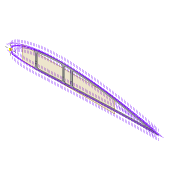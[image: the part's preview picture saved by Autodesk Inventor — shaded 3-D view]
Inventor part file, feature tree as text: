
AUTODESK INVENTOR PART (.ipt)
format: ipt  version: 2022 (Build 260153000, 153)  size: 489,984 bytes
history: native  units: mm
features: projected_geometry x8, extrude x7, sketch x7, shell x1, plane x1, chamfer x1
ambient origin geometry x8: Origin, YZ Plane, XZ Plane, XY Plane, X Axis, Y Axis, Z Axis, Center Point
bodies: Solid1 (feature_tree)
feature tree (25):
  extrude  "Extrusion1"  Depth=4.0mm
  shell  "Shell1"  Thickness=2.0mm
  extrude  "Extrusion8"  Depth=5.9mm
  extrude  "Extrusion3"  Depth=10.0mm TaperAngle=0.0deg
  extrude  "Extrusion4"  Depth=5.0mm
  extrude  "Extrusion5"  Depth=2.5mm
  plane  "Work Plane2"
  extrude  "Extrusion9"  Depth=1.6mm
  chamfer  "Chamfer1"  Distance=77.0mm
  extrude  "Extrusion12"  Depth=5.0mm
  sketch  "Sketch31"  dims[d37=5.0mm d38=1.6mm]
  sketch  "Sketch32"  dims[d40=2.5mm d62=77.0mm d63=5.0mm d64=2.0mm d65=0.0mm d66=2.5mm d67=12.0mm d68=80.0mm d69=20.0mm d70=0.5mm d71=10.0mm d72=0.0mm d75=3.0mm d76=3.0mm d77=2.0mm d78=45.0deg d80=0.0mm d81=1.0mm d82=1.0mm d83=1.0mm d84=1.0mm d85=1.0mm d88=10.0mm d89=0.0mm]
  sketch  "Sketch3"  dims[d0=2.0mm d1=0.0mm d2=4.0mm d7=2.0mm]
  sketch  "Sketch8"  dims[d8=2.0mm d9=5.9mm]
  sketch  "Sketch9"  dims[d13=10.0mm d14=0.0mm d16=10.0mm d17=0.0mm]
  projected_geometry  "Projected Loop4"
  projected_geometry  "Projected Loop10"
  sketch  "Sketch24"  dims[d22=2.0mm d23=0.0mm d32=5.0mm]
  projected_geometry  "Projected Loop11"
  projected_geometry  "Projected Loop12"
  projected_geometry  "Projected Loop13"
  sketch  "Sketch28"  dims[d34=1.6mm d35=2.5mm]
  projected_geometry  "Project Cut Edges1"
  projected_geometry  "Project Cut Edges4"
  projected_geometry  "Project Cut Edges5"
